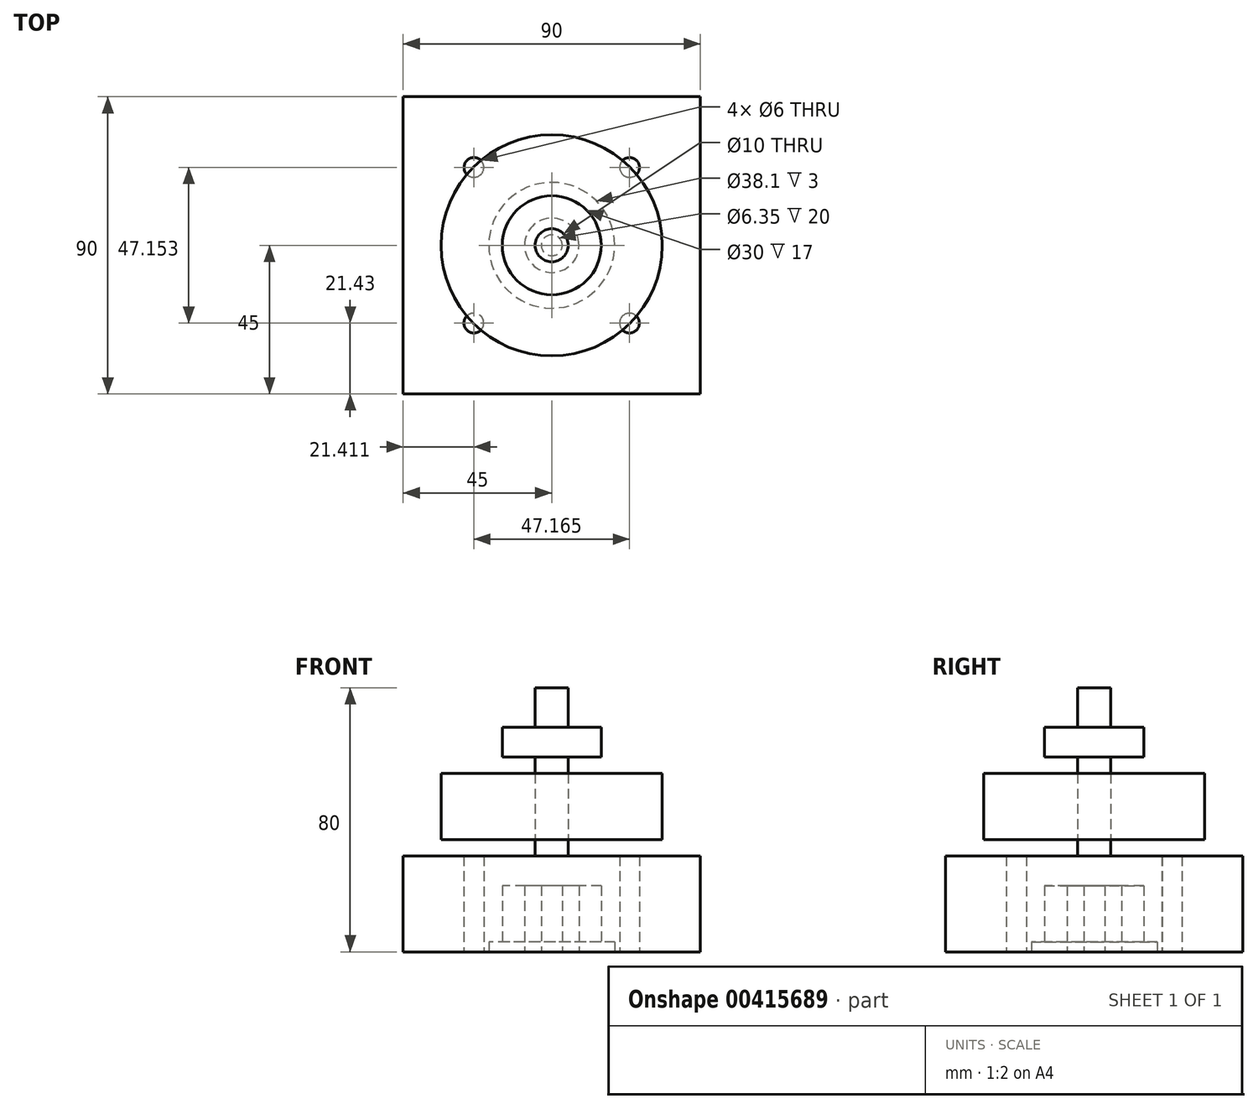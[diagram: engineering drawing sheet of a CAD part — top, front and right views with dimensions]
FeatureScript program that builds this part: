
annotation { "Feature Type Name" : "Feature", "Feature Type Description" : "" }
export const myFeature = defineFeature(function(context is Context, id is Id, definition is map)
    precondition{}
    {
        {
            var Q0;
            Q0=qCreatedBy(makeId("Top.planeOp"),FACE);
            var sketch = newSketch(context, id + "F0", { "sketchPlane" : qUnion([Q0])});
            skLineSegment(sketch, "E0.bottom", {"start": v(-35.04, 35) * mm, "end": v(34.96, 35) * mm});
            skLineSegment(sketch, "E0.top", {"start": v(-35.04, -35) * mm, "end": v(34.96, -35) * mm});
            skLineSegment(sketch, "E0.left", {"start": v(-35.04, 35) * mm, "end": v(-35.04, -35) * mm});
            skLineSegment(sketch, "E0.right", {"start": v(34.96, 35) * mm, "end": v(34.96, -35) * mm});
            skCircle(sketch, "E1", {"center": v(-23.54, -23.5) * mm, "radius": 3 * mm});
            skCircle(sketch, "E2", {"center": v(-23.54, 23.5) * mm, "radius": 3 * mm});
            skCircle(sketch, "E3", {"center": v(23.46, -23.5) * mm, "radius": 3 * mm});
            skCircle(sketch, "E4", {"center": v(23.82, 23.5) * mm, "radius": 3 * mm});
            skCircle(sketch, "E5", {"center": v(-0.04, 0) * mm, "radius": 15 * mm});
            skCircle(sketch, "E6", {"center": v(0, 0) * mm, "radius": 19.05 * mm});
            skSolve(sketch);
        }
        {
            var Q0;
            Q0=qCreatedBy(makeId("Top.planeOp"),FACE);
            var sketch = newSketch(context, id + "F1", { "sketchPlane" : qUnion([Q0])});
            skLineSegment(sketch, "E7.bottom", {"start": v(45, -45) * mm, "end": v(-45, -45) * mm});
            skLineSegment(sketch, "E7.top", {"start": v(45, 45) * mm, "end": v(-45, 45) * mm});
            skLineSegment(sketch, "E7.left", {"start": v(45, -45) * mm, "end": v(45, 45) * mm});
            skLineSegment(sketch, "E7.right", {"start": v(-45, -45) * mm, "end": v(-45, 45) * mm});
            skPoint(sketch, "E7.middle", {"position": v(0, 0) * mm});
            skCircle(sketch, "E8", {"center": v(0, 0) * mm, "radius": 15 * mm});
            skCircle(sketch, "E9", {"center": v(0, 0) * mm, "radius": 19.05 * mm});
            skCircle(sketch, "E10", {"center": v(0, 0) * mm, "radius": 33.34 * mm, "construction": true});
            skCircle(sketch, "E11", {"center": v(-23.56, 23.58) * mm, "radius": 3 * mm});
            skCircle(sketch, "E12", {"center": v(23.58, 23.57) * mm, "radius": 3 * mm});
            skCircle(sketch, "E13", {"center": v(23.55, -23.57) * mm, "radius": 3 * mm});
            skCircle(sketch, "E14", {"center": v(-23.59, -23.56) * mm, "radius": 3 * mm});
            skSolve(sketch);
        }
        {
            var Q0;
            Q0=qCreatedBy(makeId("Top.planeOp"),FACE);
            var sketch = newSketch(context, id + "F2", { "sketchPlane" : qUnion([Q0])});
            skCircle(sketch, "E15", {"center": v(0, 0) * mm, "radius": 5 * mm});
            skCircle(sketch, "E16", {"center": v(0, 0) * mm, "radius": 8.25 * mm});
            skCircle(sketch, "E17", {"center": v(0, 0) * mm, "radius": 3.17 * mm});
            skSolve(sketch);
        }
        {
            var Q0;
            Q0=makeQuery(id+"F2.imprint","IMPRINT",FACE,{"disambiguationData":[TD([[makeQuery(id+"F2.imprint","IMPRINT",EDGE,{"derivedFrom":sQuery(id+"F2.wireOp",EDGE,"E15")}),-1.0]])]});
            var Q1;
            Q1=makeQuery(id+"F2.imprint","IMPRINT",FACE,{"disambiguationData":[TD([[makeQuery(id+"F2.imprint","IMPRINT",EDGE,{"derivedFrom":sQuery(id+"F2.wireOp",EDGE,"E15")}),1.0]])]});
            extrude(context, id + "F3", {"entities" : qUnion([Q0, Q1]), "depth" : 20 * mm});
        }
        {
            var Q0;
            Q0=makeQuery(id+"F2.imprint","IMPRINT",FACE,{"disambiguationData":[TD([[makeQuery(id+"F2.imprint","IMPRINT",EDGE,{"derivedFrom":sQuery(id+"F2.wireOp",EDGE,"E15")}),1.0]])]});
            var Q1;
            Q1=makeQuery(id+"F2.imprint","IMPRINT",FACE,{"disambiguationData":[TD([[makeQuery(id+"F2.imprint","IMPRINT",EDGE,{"derivedFrom":sQuery(id+"F2.wireOp",EDGE,"E17")}),1.0]])]});
            extrude(context, id + "F4", {"entities" : qUnion([Q0, Q1]), "operationType" : NewBodyOperationType.ADD, "depth" : 80 * mm, "hasSecondDirection" : true, "secondDirectionOppositeDirection" : true, "secondDirectionDepth" : -20 * mm});
        }
        {
            var Q0;
            Q0=qCreatedBy(makeId("Top.planeOp"),FACE);
            var sketch = newSketch(context, id + "F5", { "sketchPlane" : qUnion([Q0])});
            skCircle(sketch, "E18", {"center": v(0, 0) * mm, "radius": 15 * mm});
            skCircle(sketch, "E19", {"center": v(0, 0) * mm, "radius": 5 * mm});
            skSolve(sketch);
        }
        {
            var Q0;
            Q0 = qSketchRegion(id + "F5", true);
            extrude(context, id + "F6", {"entities" : qUnion([Q0]), "operationType" : NewBodyOperationType.ADD, "depth" : 29 * mm, "hasSecondDirection" : true, "secondDirectionOppositeDirection" : false, "secondDirectionDepth" : 20 * mm});
        }
        {
            var Q0;
            Q0=makeQuery(id+"F6.opExtrude","CAP_FACE",FACE,{"disambiguationData":[OSD([sQuery(id+"F5.wireOp",EDGE,"E18"),sQuery(id+"F5.wireOp",EDGE,"E19")])],"isStart":false});
            extrude(context, id + "F7", {"entities" : qUnion([Q0]), "operationType" : NewBodyOperationType.ADD, "depth" : 39 * mm, "hasSecondDirection" : true, "secondDirectionOppositeDirection" : false, "secondDirectionDepth" : 30 * mm});
        }
        {
            var Q0;
            Q0=qCreatedBy(makeId("Top.planeOp"),FACE);
            var sketch = newSketch(context, id + "F8", { "sketchPlane" : qUnion([Q0])});
            skCircle(sketch, "E20", {"center": v(0, 0) * mm, "radius": 33.5 * mm});
            skCircle(sketch, "E21", {"center": v(0, 0) * mm, "radius": 5 * mm});
            skSolve(sketch);
        }
        {
            var Q0;
            Q0 = qSketchRegion(id + "F8", true);
            var Q1;
            Q1=makeQuery(id+"F3.opExtrude","SWEPT_BODY",BODY,{"disambiguationData":[OSD([sQuery(id+"F2.wireOp",EDGE,"E16"),sQuery(id+"F2.wireOp",EDGE,"E17")])]});
            extrude(context, id + "F9", {"entities" : qUnion([Q0]), "endBoundEntityBody" : qUnion([Q1]), "depth" : 54 * mm, "hasSecondDirection" : true, "secondDirectionOppositeDirection" : false, "secondDirectionDepth" : 34 * mm});
        }
        {
            var Q0;
            Q0=makeQuery(id+"F1.imprint","IMPRINT",FACE,{"disambiguationData":[TD([[makeQuery(id+"F1.imprint","IMPRINT",EDGE,{"derivedFrom":sQuery(id+"F1.wireOp",EDGE,"E8")}),-1.0]])]});
            var Q1;
            Q1=makeQuery(id+"F1.imprint","IMPRINT",FACE,{"disambiguationData":[TD([[makeQuery(id+"F1.imprint","IMPRINT",EDGE,{"derivedFrom":sQuery(id+"F1.wireOp",EDGE,"E7.bottom")}),-1.0]])]});
            extrude(context, id + "F10", {"entities" : qUnion([Q0, Q1]), "operationType" : NewBodyOperationType.ADD, "depth" : 29 * mm, "hasSecondDirection" : true, "secondDirectionOppositeDirection" : false, "secondDirectionDepth" : 3 * mm});
        }
        {
            var Q0;
            Q0=makeQuery(id+"F1.imprint","IMPRINT",FACE,{"disambiguationData":[TD([[makeQuery(id+"F1.imprint","IMPRINT",EDGE,{"derivedFrom":sQuery(id+"F1.wireOp",EDGE,"E7.bottom")}),-1.0]])]});
            extrude(context, id + "F11", {"entities" : qUnion([Q0]), "operationType" : NewBodyOperationType.ADD, "depth" : 3 * mm});
        }
    });
